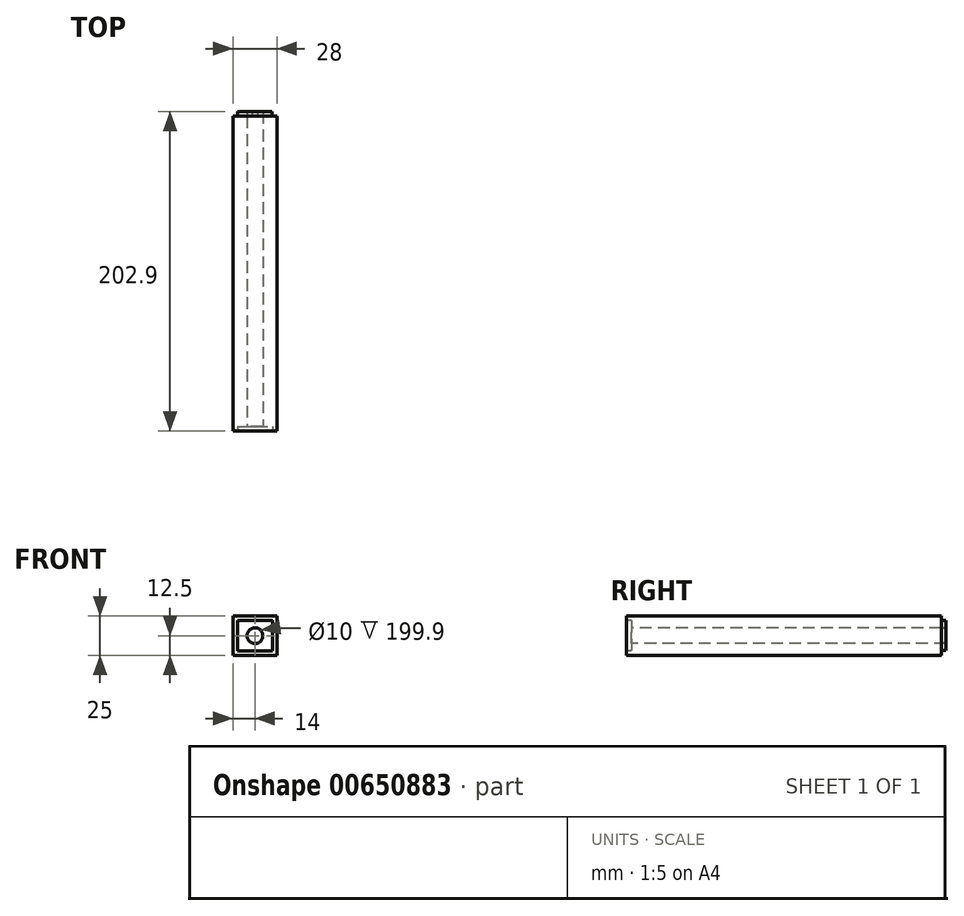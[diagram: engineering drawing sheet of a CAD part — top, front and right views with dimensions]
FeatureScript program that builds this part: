
annotation { "Feature Type Name" : "Feature", "Feature Type Description" : "" }
export const myFeature = defineFeature(function(context is Context, id is Id, definition is map)
    precondition{}
    {
        {
            var Q0;
            Q0=qCreatedBy(makeId("Front.planeOp"),FACE);
            var sketch = newSketch(context, id + "F0", { "sketchPlane" : qUnion([Q0])});
            skLineSegment(sketch, "E0.bottom", {"start": v(-14, 12.5) * mm, "end": v(14, 12.5) * mm});
            skLineSegment(sketch, "E0.top", {"start": v(-14, -12.5) * mm, "end": v(14, -12.5) * mm});
            skLineSegment(sketch, "E0.left", {"start": v(-14, 12.5) * mm, "end": v(-14, -12.5) * mm});
            skLineSegment(sketch, "E0.right", {"start": v(14, 12.5) * mm, "end": v(14, -12.5) * mm});
            skLineSegment(sketch, "E1.bottom", {"start": v(-11.1, 9.6) * mm, "end": v(11.1, 9.6) * mm});
            skLineSegment(sketch, "E1.top", {"start": v(-11.1, -9.6) * mm, "end": v(11.1, -9.6) * mm});
            skLineSegment(sketch, "E1.left", {"start": v(-11.1, 9.6) * mm, "end": v(-11.1, -9.6) * mm});
            skLineSegment(sketch, "E1.right", {"start": v(11.1, 9.6) * mm, "end": v(11.1, -9.6) * mm});
            skCircle(sketch, "E2", {"center": v(0, 0) * mm, "radius": 5 * mm});
            skSolve(sketch);
        }
        {
            var Q0;
            Q0=makeQuery(id+"F0.imprint","IMPRINT",FACE,{"disambiguationData":[TD([[makeQuery(id+"F0.imprint","IMPRINT",EDGE,{"derivedFrom":sQuery(id+"F0.wireOp",EDGE,"E1.bottom")}),-1.0]])]});
            var Q1;
            Q1=makeQuery(id+"F0.imprint","IMPRINT",FACE,{"disambiguationData":[TD([[makeQuery(id+"F0.imprint","IMPRINT",EDGE,{"derivedFrom":sQuery(id+"F0.wireOp",EDGE,"E0.bottom")}),-1.0]])]});
            extrude(context, id + "F1", {"entities" : qUnion([Q0, Q1]), "oppositeDirection" : true, "depth" : 200 * mm, "offsetDistance" : 25 * mm});
        }
        {
            var Q0;
            Q0=makeQuery(id+"F0.imprint","IMPRINT",FACE,{"disambiguationData":[TD([[makeQuery(id+"F0.imprint","IMPRINT",EDGE,{"derivedFrom":sQuery(id+"F0.wireOp",EDGE,"E1.bottom")}),-1.0]])]});
            extrude(context, id + "F2", {"entities" : qUnion([Q0]), "operationType" : NewBodyOperationType.REMOVE, "oppositeDirection" : true, "depth" : 3 * mm, "offsetDistance" : 25 * mm});
        }
        {
            var Q0;
            Q0=makeQuery(id+"F1.opExtrude","CAP_FACE",FACE,{"disambiguationData":[OSD([sQuery(id+"F0.wireOp",EDGE,"E0.bottom"),sQuery(id+"F0.wireOp",EDGE,"E0.top"),sQuery(id+"F0.wireOp",EDGE,"E0.left"),sQuery(id+"F0.wireOp",EDGE,"E0.right"),sQuery(id+"F0.wireOp",EDGE,"E2")])],"isStart":false});
            var sketch = newSketch(context, id + "F3", { "sketchPlane" : qUnion([Q0])});
            skCircle(sketch, "E3", {"center": v(0.12, 0.04) * mm, "radius": 5 * mm});
            skLineSegment(sketch, "E4.bottom", {"start": v(-10.88, 9.54) * mm, "end": v(11.12, 9.54) * mm});
            skLineSegment(sketch, "E4.top", {"start": v(-10.88, -9.46) * mm, "end": v(11.12, -9.46) * mm});
            skLineSegment(sketch, "E4.left", {"start": v(-10.88, 9.54) * mm, "end": v(-10.88, -9.46) * mm});
            skLineSegment(sketch, "E4.right", {"start": v(11.12, 9.54) * mm, "end": v(11.12, -9.46) * mm});
            skSolve(sketch);
        }
        {
            var Q0;
            Q0=makeQuery(id+"F3.imprint","IMPRINT",FACE,{"disambiguationData":[TD([[makeQuery(id+"F3.imprint","IMPRINT",EDGE,{"derivedFrom":sQuery(id+"F3.wireOp",EDGE,"E4.bottom")}),-1.0]])]});
            extrude(context, id + "F4", {"entities" : qUnion([Q0]), "operationType" : NewBodyOperationType.ADD, "depth" : 2.9 * mm, "offsetDistance" : 25 * mm});
        }
    });
